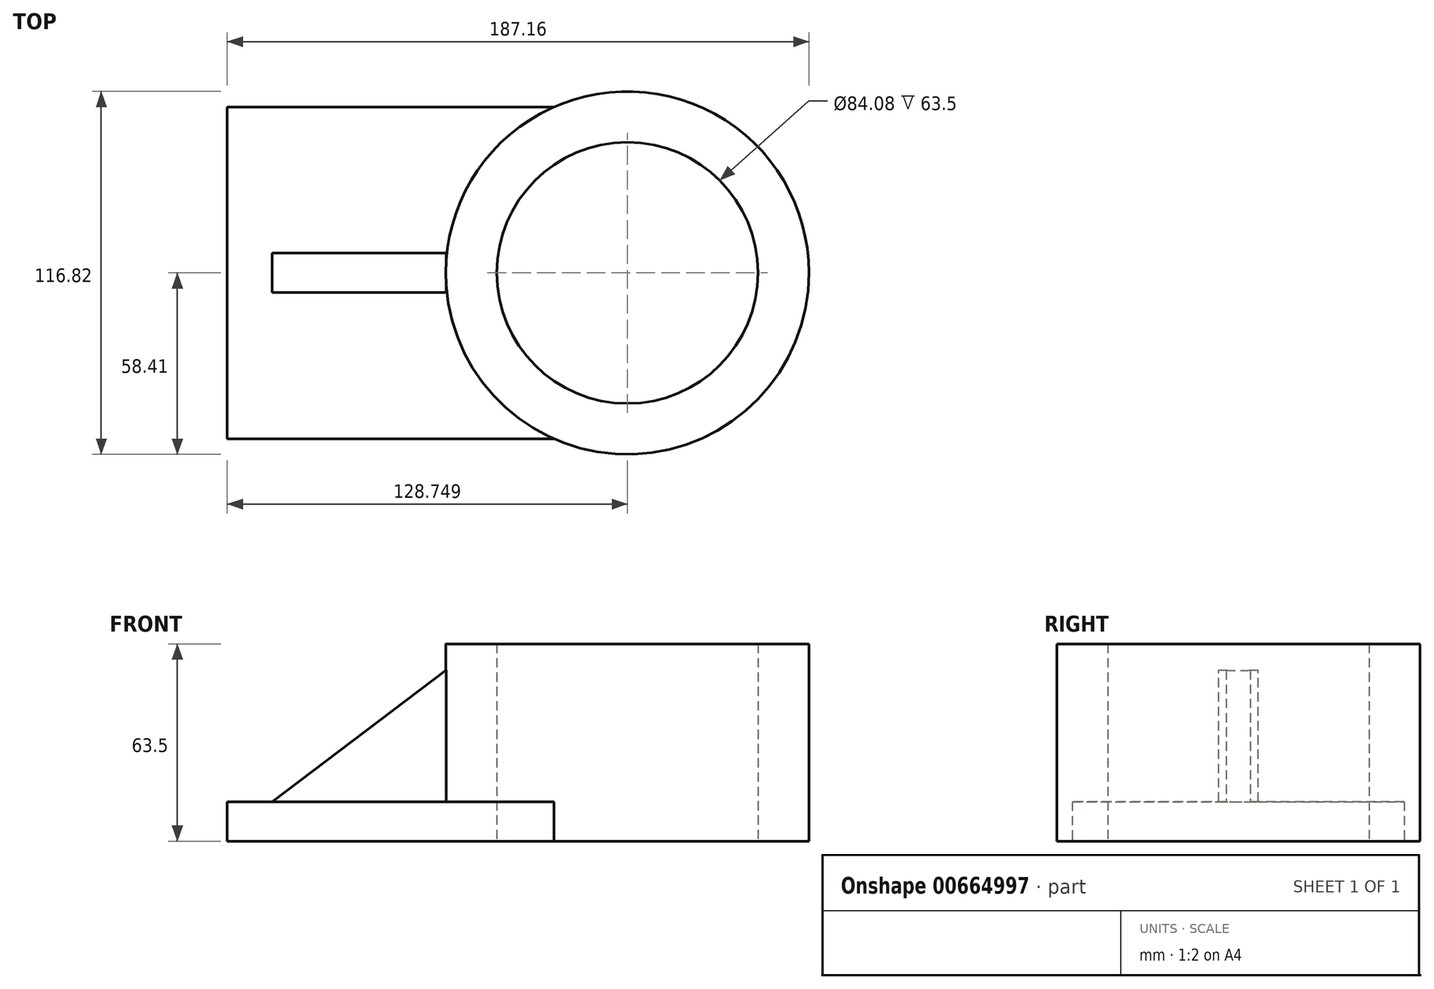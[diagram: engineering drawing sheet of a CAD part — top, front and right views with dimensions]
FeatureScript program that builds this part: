
annotation { "Feature Type Name" : "Feature", "Feature Type Description" : "" }
export const myFeature = defineFeature(function(context is Context, id is Id, definition is map)
    precondition{}
    {
        {
            var Q0;
            Q0=qCreatedBy(makeId("Top.planeOp"),FACE);
            var sketch = newSketch(context, id + "F0", { "sketchPlane" : qUnion([Q0])});
            skCircle(sketch, "E0", {"center": v(76.2, 0) * mm, "radius": 58.41 * mm});
            skCircle(sketch, "E1", {"center": v(76.2, 0) * mm, "radius": 42.04 * mm});
            skLineSegment(sketch, "E2.bottom", {"start": v(52.55, -53.41) * mm, "end": v(-52.55, -53.41) * mm});
            skLineSegment(sketch, "E2.top", {"start": v(52.55, 53.41) * mm, "end": v(-52.55, 53.41) * mm});
            skLineSegment(sketch, "E2.right", {"start": v(-52.55, -53.41) * mm, "end": v(-52.55, 53.41) * mm});
            skPoint(sketch, "E2.middle", {"position": v(0, 0) * mm});
            skSolve(sketch);
        }
        {
            var Q0;
            Q0=makeQuery(id+"F0.imprint","IMPRINT",FACE,{"disambiguationData":[TD([[makeQuery(id+"F0.imprint","IMPRINT",EDGE,{"derivedFrom":sQuery(id+"F0.wireOp",EDGE,"E1")}),-1.0]])]});
            extrude(context, id + "F1", {"entities" : qUnion([Q0]), "depth" : 63.5 * mm, "offsetDistance" : 25.4 * mm});
        }
        {
            var Q0;
            {var subQ0=sQuery(id+"F0.wireOp",EDGE,"E2.bottom");Q0=makeQuery(id+"F0.imprint","IMPRINT",FACE,{"disambiguationData":[TD([[makeQuery(id+"F0.imprint","IMPRINT",EDGE,{"derivedFrom":subQ0}),-1.0]])]});}
            extrude(context, id + "F2", {"entities" : qUnion([Q0]), "operationType" : NewBodyOperationType.ADD, "depth" : 12.7 * mm, "offsetDistance" : 25.4 * mm});
        }
        {
            var Q0;
            Q0=qCreatedBy(makeId("Front.planeOp"),FACE);
            var sketch = newSketch(context, id + "F3", { "sketchPlane" : qUnion([Q0])});
            skLineSegment(sketch, "E3", {"start": v(17.92, 55.03) * mm, "end": v(-38.82, 12.18) * mm});
            skLineSegment(sketch, "E4", {"start": v(-38.82, 12.18) * mm, "end": v(17.92, 12.18) * mm});
            skLineSegment(sketch, "E5", {"start": v(17.92, 12.18) * mm, "end": v(17.92, 55.03) * mm});
            skSolve(sketch);
        }
        {
            var Q0;
            Q0 = qSketchRegion(id + "F3", true);
            extrude(context, id + "F4", {"entities" : qUnion([Q0]), "operationType" : NewBodyOperationType.ADD, "endBound" : BoundingType.SYMMETRIC, "depth" : 12.7 * mm, "offsetDistance" : 25.4 * mm});
        }
    });
